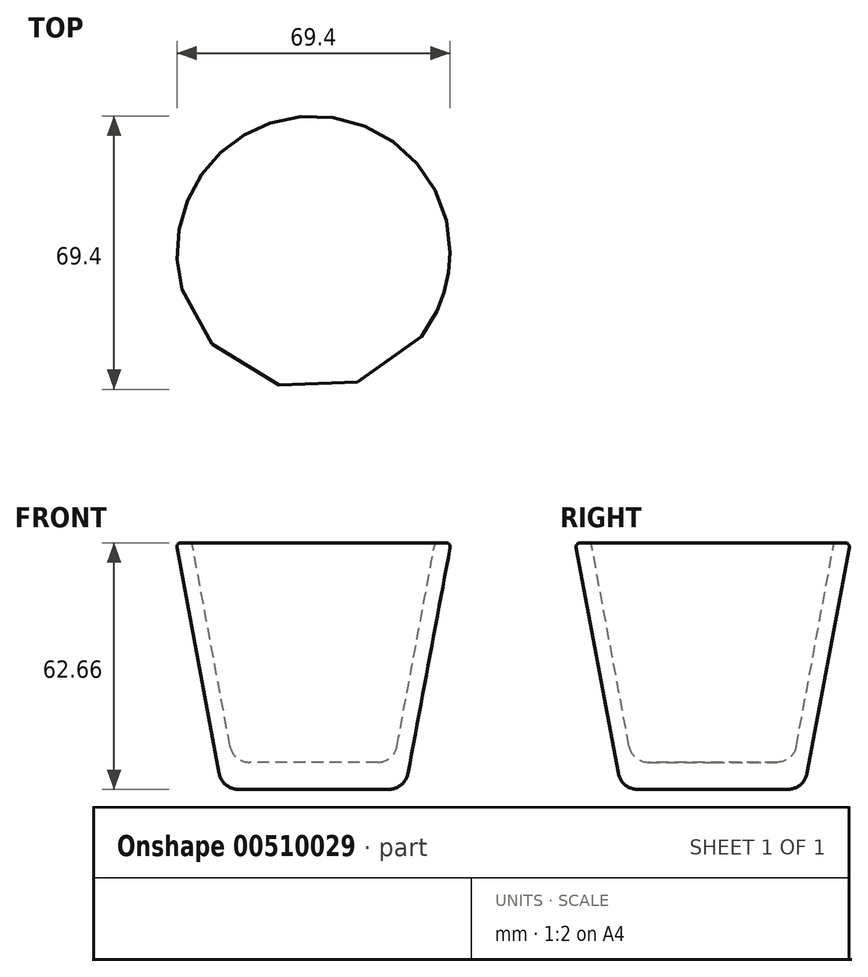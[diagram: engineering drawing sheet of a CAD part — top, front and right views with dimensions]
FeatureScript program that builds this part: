
annotation { "Feature Type Name" : "Feature", "Feature Type Description" : "" }
export const myFeature = defineFeature(function(context is Context, id is Id, definition is map)
    precondition{}
    {
        {
            var Q0;
            Q0=qCreatedBy(makeId("Front.planeOp"),FACE);
            var sketch = newSketch(context, id + "F0", { "sketchPlane" : qUnion([Q0])});
            skLineSegment(sketch, "E0", {"start": v(0, -21.08) * mm, "end": v(19.06, -21.08) * mm});
            skLineSegment(sketch, "E1", {"start": v(23.98, -17) * mm, "end": v(34.69, 40.4) * mm});
            skLineSegment(sketch, "E2", {"start": v(33.7, 41.58) * mm, "end": v(31.7, 41.58) * mm});
            skLineSegment(sketch, "E3", {"start": v(30.72, 40.76) * mm, "end": v(21.23, -10.1) * mm});
            skLineSegment(sketch, "E4", {"start": v(16.31, -14.2) * mm, "end": v(0, -14.2) * mm});
            skPoint(sketch, "E5.visualSharp", {"position": v(20.47, -14.2) * mm});
            skArc(sketch, "E5.filletArc", {"start": v(16.31, -14.2) * mm, "mid": v(19.5, -13.04) * mm, "end": v(21.23, -10.1) * mm});
            skPoint(sketch, "E6.visualSharp", {"position": v(23.22, -21.08) * mm});
            skArc(sketch, "E6.filletArc", {"start": v(19.06, -21.08) * mm, "mid": v(22.26, -19.93) * mm, "end": v(23.98, -17) * mm});
            skPoint(sketch, "E7.visualSharp", {"position": v(30.87, 41.58) * mm});
            skArc(sketch, "E7.filletArc", {"start": v(31.7, 41.58) * mm, "mid": v(31.07, 41.35) * mm, "end": v(30.72, 40.76) * mm});
            skPoint(sketch, "E8.visualSharp", {"position": v(34.9, 41.58) * mm});
            skArc(sketch, "E8.filletArc", {"start": v(34.69, 40.4) * mm, "mid": v(34.47, 41.22) * mm, "end": v(33.7, 41.58) * mm});
            skLineSegment(sketch, "E9", {"start": v(0, -14.2) * mm, "end": v(0, -21.08) * mm});
            skSolve(sketch);
        }
        {
            var Q0;
            Q0=makeQuery(id+"F0.imprint","IMPRINT",FACE,{"disambiguationData":[TD([[makeQuery(id+"F0.imprint","IMPRINT",EDGE,{"derivedFrom":sQuery(id+"F0.wireOp",EDGE,"E0")}),1.0]])]});
            var Q1;
            Q1=sQuery(id+"F0.wireOp",EDGE,"E9");
            revolve(context, id + "F1", {"entities" : qUnion([Q0]), "axis" : qUnion([Q1]), "revolveType" : RevolveType.FULL});
        }
    });
